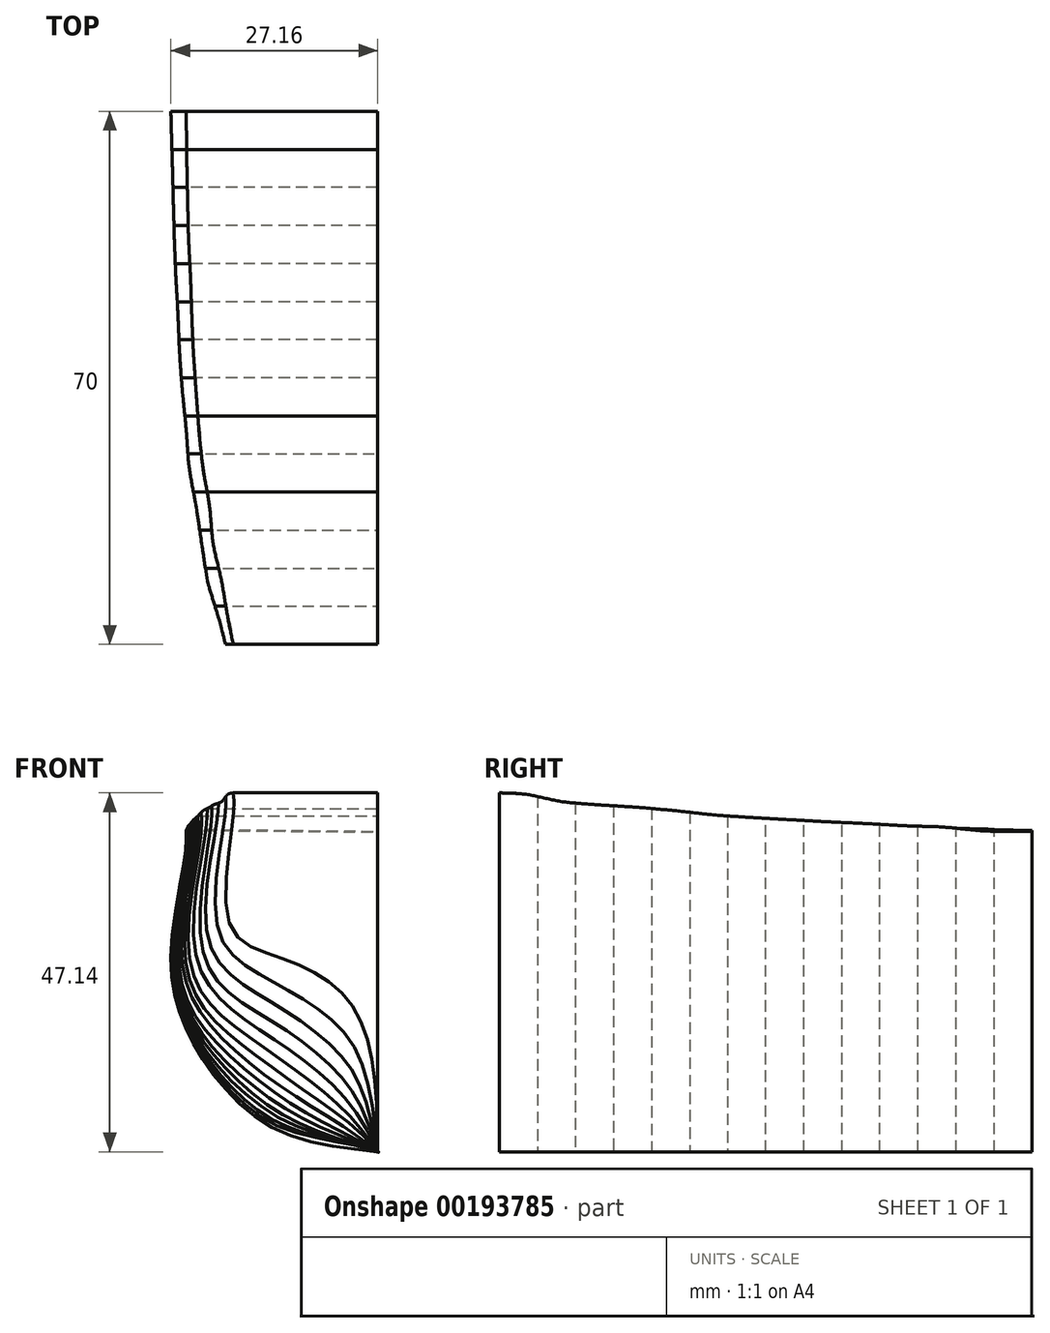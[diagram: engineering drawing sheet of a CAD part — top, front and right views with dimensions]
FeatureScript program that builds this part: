
annotation { "Feature Type Name" : "Feature", "Feature Type Description" : "" }
export const myFeature = defineFeature(function(context is Context, id is Id, definition is map)
    precondition{}
    {
        {
            var Q0;
            Q0=qCreatedBy(makeId("Front.planeOp"),FACE);
            var sketch = newSketch(context, id + "F0", { "sketchPlane" : qUnion([Q0])});
            skLineSegment(sketch, "E0", {"start": v(-1.24, 24.74) * mm, "end": v(-1.24, -22.4) * mm});
            skFitSpline(sketch, "E1", {"points": [v(-1.24, -22.4) * mm, v(-14.07, -19.7) * mm, v(-22.33, -12.84) * mm, v(-26.84, -5.13) * mm, v(-28.38, 3.95) * mm, v(-26.49, 16.94) * mm, v(-26.4, 19.83) * mm], "startDerivative": vector(-68.68, 7.38) * mm, "endDerivative": vector(-1.29, 24.48) * mm});
            skLineSegment(sketch, "E2", {"start": v(-26.4, 19.83) * mm, "end": v(-1.24, 19.58) * mm});
            skSolve(sketch);
        }
        {
            var Q0;
            Q0=qCreatedBy(makeId("Front.planeOp"),FACE);
            cPlane(context, id + "F1", {"entities" : qUnion([Q0]), "cplaneType" : CPlaneType.OFFSET, "offset" : 5 * mm, "width" : 150 * mm, "height" : 150 * mm});
        }
        {
            var Q0;
            Q0=qCreatedBy(id+"F1.planeOp",FACE);
            var sketch = newSketch(context, id + "F2", { "sketchPlane" : qUnion([Q0])});
            skLineSegment(sketch, "E3", {"start": v(-1.24, 24.74) * mm, "end": v(-1.24, -22.4) * mm});
            skFitSpline(sketch, "E4", {"points": [v(-1.24, -22.4) * mm, v(-13.68, -19.3) * mm, v(-22.09, -12.65) * mm, v(-26.68, -5.02) * mm, v(-28.23, 4.02) * mm, v(-26.4, 17.02) * mm, v(-26.33, 19.94) * mm], "startDerivative": vector(-61.26, 21.5) * mm, "endDerivative": vector(-1.44, 24.58) * mm});
            skLineSegment(sketch, "E5", {"start": v(-26.33, 19.94) * mm, "end": v(-1.24, 19.7) * mm});
            skSolve(sketch);
        }
        {
            var Q0;
            {var subQ0=sQuery(id+"F0.wireOp",EDGE,"E1");Q0=makeQuery(id+"F0.imprint","IMPRINT",FACE,{"disambiguationData":[TD([[makeQuery(id+"F0.imprint","IMPRINT",EDGE,{"derivedFrom":subQ0}),-1.0]])]});}
            var Q1;
            {var subQ0=sQuery(id+"F2.wireOp",EDGE,"E4");Q1=makeQuery(id+"F2.imprint","IMPRINT",FACE,{"disambiguationData":[TD([[makeQuery(id+"F2.imprint","IMPRINT",EDGE,{"derivedFrom":subQ0}),-1.0]])]});}
            loft(context, id + "F3", {"sheetProfilesArray" : [{ "sheetProfileEntities" : qUnion([Q0]) }, { "sheetProfileEntities" : qUnion([Q1]) }]});
        }
        {
            var Q0;
            Q0=qCreatedBy(id+"F1.planeOp",FACE);
            cPlane(context, id + "F4", {"entities" : qUnion([Q0]), "cplaneType" : CPlaneType.OFFSET, "offset" : 5 * mm, "width" : 150 * mm, "height" : 150 * mm});
        }
        {
            var Q0;
            Q0=qCreatedBy(id+"F4.planeOp",FACE);
            var sketch = newSketch(context, id + "F5", { "sketchPlane" : qUnion([Q0])});
            skLineSegment(sketch, "E6", {"start": v(-1.24, 24.74) * mm, "end": v(-1.24, -22.4) * mm});
            skFitSpline(sketch, "E7", {"points": [v(-1.24, -22.4) * mm, v(-13.39, -19) * mm, v(-21.77, -12.4) * mm, v(-26.53, -4.92) * mm, v(-28.1, 4.08) * mm, v(-26.3, 17.1) * mm, v(-26.23, 20.09) * mm], "startDerivative": vector(-61.65, 21.65) * mm, "endDerivative": vector(-1.33, 24.82) * mm});
            skLineSegment(sketch, "E8", {"start": v(-26.23, 20.09) * mm, "end": v(-1.24, 20.09) * mm});
            skSolve(sketch);
        }
        {
            var Q1;
            {var subQ0=sQuery(id+"F2.wireOp",EDGE,"E4");Q1=makeQuery(id+"F3.opLoft","CAP_FACE",FACE,{"disambiguationData":[OSD([makeQuery(id+"F2.imprint","IMPRINT",FACE,{"disambiguationData":[TD([[makeQuery(id+"F2.imprint","IMPRINT",EDGE,{"derivedFrom":subQ0}),-1.0]])]})])],"isStart":true});}
            var Q2;
            {var subQ0=sQuery(id+"F5.wireOp",EDGE,"E7");Q2=makeQuery(id+"F5.imprint","IMPRINT",FACE,{"disambiguationData":[TD([[makeQuery(id+"F5.imprint","IMPRINT",EDGE,{"derivedFrom":subQ0}),-1.0]])]});}
            loft(context, id + "F6", {"operationType" : NewBodyOperationType.ADD, "startCondition" : LoftEndDerivativeType.MATCH_CURVATURE, "startMagnitude" : 1, "sheetProfilesArray" : [{ "sheetProfileEntities" : qUnion([Q1]) }, { "sheetProfileEntities" : qUnion([Q2]) }]});
        }
        {
            var Q0;
            Q0=qCreatedBy(id+"F4.planeOp",FACE);
            cPlane(context, id + "F7", {"entities" : qUnion([Q0]), "cplaneType" : CPlaneType.OFFSET, "offset" : 5 * mm, "width" : 150 * mm, "height" : 150 * mm});
        }
        {
            var Q0;
            Q0=qCreatedBy(id+"F7.planeOp",FACE);
            var sketch = newSketch(context, id + "F8", { "sketchPlane" : qUnion([Q0])});
            skLineSegment(sketch, "E9", {"start": v(-1.24, 24.74) * mm, "end": v(-1.24, -22.4) * mm});
            skFitSpline(sketch, "E10", {"points": [v(-1.24, -22.4) * mm, v(-12.95, -18.55) * mm, v(-21.39, -12.08) * mm, v(-26.33, -4.78) * mm, v(-27.97, 4.13) * mm, v(-26.2, 17.21) * mm, v(-26.12, 20.36) * mm], "startDerivative": vector(-62.32, 21.88) * mm, "endDerivative": vector(-1.45, 25.67) * mm});
            skLineSegment(sketch, "E11", {"start": v(-26.12, 20.36) * mm, "end": v(-1.24, 20.36) * mm});
            skSolve(sketch);
        }
        {
            var Q1;
            {var subQ0=sQuery(id+"F5.wireOp",EDGE,"E7");Q1=makeQuery(id+"F6.opLoft","CAP_FACE",FACE,{"disambiguationData":[OSD([makeQuery(id+"F5.imprint","IMPRINT",FACE,{"disambiguationData":[TD([[makeQuery(id+"F5.imprint","IMPRINT",EDGE,{"derivedFrom":subQ0}),-1.0]])]})])],"isStart":true});}
            var Q2;
            {var subQ0=sQuery(id+"F8.wireOp",EDGE,"E10");Q2=makeQuery(id+"F8.imprint","IMPRINT",FACE,{"disambiguationData":[TD([[makeQuery(id+"F8.imprint","IMPRINT",EDGE,{"derivedFrom":subQ0}),-1.0]])]});}
            loft(context, id + "F9", {"operationType" : NewBodyOperationType.ADD, "startCondition" : LoftEndDerivativeType.MATCH_CURVATURE, "startMagnitude" : 1, "sheetProfilesArray" : [{ "sheetProfileEntities" : qUnion([Q1]) }, { "sheetProfileEntities" : qUnion([Q2]) }]});
        }
        {
            var Q0;
            Q0=qCreatedBy(id+"F7.planeOp",FACE);
            cPlane(context, id + "F10", {"entities" : qUnion([Q0]), "cplaneType" : CPlaneType.OFFSET, "offset" : 5 * mm, "width" : 150 * mm, "height" : 150 * mm});
        }
        {
            var Q0;
            Q0=qCreatedBy(id+"F10.planeOp",FACE);
            var sketch = newSketch(context, id + "F11", { "sketchPlane" : qUnion([Q0])});
            skLineSegment(sketch, "E12", {"start": v(-1.24, 24.74) * mm, "end": v(-1.24, -22.4) * mm});
            skFitSpline(sketch, "E13", {"points": [v(-1.24, -22.4) * mm, v(-12.54, -18.13) * mm, v(-20.94, -11.72) * mm, v(-26.08, -4.6) * mm, v(-27.8, 4.2) * mm, v(-26.01, 17.39) * mm, v(-25.9, 20.6) * mm], "startDerivative": vector(-62.84, 22.07) * mm, "endDerivative": vector(-1.04, 25.92) * mm});
            skLineSegment(sketch, "E14", {"start": v(-25.9, 20.6) * mm, "end": v(-1.24, 20.6) * mm});
            skSolve(sketch);
        }
        {
            var Q1;
            {var subQ0=sQuery(id+"F8.wireOp",EDGE,"E10");Q1=makeQuery(id+"F9.opLoft","CAP_FACE",FACE,{"disambiguationData":[OSD([makeQuery(id+"F8.imprint","IMPRINT",FACE,{"disambiguationData":[TD([[makeQuery(id+"F8.imprint","IMPRINT",EDGE,{"derivedFrom":subQ0}),-1.0]])]})])],"isStart":true});}
            var Q2;
            {var subQ0=sQuery(id+"F11.wireOp",EDGE,"E13");Q2=makeQuery(id+"F11.imprint","IMPRINT",FACE,{"disambiguationData":[TD([[makeQuery(id+"F11.imprint","IMPRINT",EDGE,{"derivedFrom":subQ0}),-1.0]])]});}
            loft(context, id + "F12", {"operationType" : NewBodyOperationType.ADD, "startCondition" : LoftEndDerivativeType.MATCH_CURVATURE, "startMagnitude" : 1, "sheetProfilesArray" : [{ "sheetProfileEntities" : qUnion([Q1]) }, { "sheetProfileEntities" : qUnion([Q2]) }]});
        }
        {
            var Q0;
            Q0=qCreatedBy(id+"F10.planeOp",FACE);
            cPlane(context, id + "F13", {"entities" : qUnion([Q0]), "cplaneType" : CPlaneType.OFFSET, "offset" : 5 * mm, "width" : 150 * mm, "height" : 150 * mm});
        }
        {
            var Q0;
            Q0=qCreatedBy(id+"F13.planeOp",FACE);
            var sketch = newSketch(context, id + "F14", { "sketchPlane" : qUnion([Q0])});
            skLineSegment(sketch, "E15", {"start": v(-1.24, 24.74) * mm, "end": v(-1.24, -22.4) * mm});
            skFitSpline(sketch, "E16", {"points": [v(-1.24, -22.4) * mm, v(-11.95, -17.53) * mm, v(-20.41, -11.29) * mm, v(-25.78, -4.4) * mm, v(-27.54, 4.32) * mm, v(-25.82, 17.59) * mm, v(-25.7, 20.85) * mm], "startDerivative": vector(-63.96, 28.52) * mm, "endDerivative": vector(-0.98, 26.03) * mm});
            skLineSegment(sketch, "E17", {"start": v(-25.7, 20.85) * mm, "end": v(-1.24, 20.85) * mm});
            skSolve(sketch);
        }
        {
            var Q1;
            {var subQ0=sQuery(id+"F11.wireOp",EDGE,"E13");Q1=makeQuery(id+"F12.opLoft","CAP_FACE",FACE,{"disambiguationData":[OSD([makeQuery(id+"F11.imprint","IMPRINT",FACE,{"disambiguationData":[TD([[makeQuery(id+"F11.imprint","IMPRINT",EDGE,{"derivedFrom":subQ0}),-1.0]])]})])],"isStart":true});}
            var Q2;
            {var subQ0=sQuery(id+"F14.wireOp",EDGE,"E16");Q2=makeQuery(id+"F14.imprint","IMPRINT",FACE,{"disambiguationData":[TD([[makeQuery(id+"F14.imprint","IMPRINT",EDGE,{"derivedFrom":subQ0}),-1.0]])]});}
            loft(context, id + "F15", {"operationType" : NewBodyOperationType.ADD, "startCondition" : LoftEndDerivativeType.MATCH_CURVATURE, "startMagnitude" : 1, "sheetProfilesArray" : [{ "sheetProfileEntities" : qUnion([Q1]) }, { "sheetProfileEntities" : qUnion([Q2]) }]});
        }
        {
            var Q0;
            Q0=qCreatedBy(id+"F13.planeOp",FACE);
            cPlane(context, id + "F16", {"entities" : qUnion([Q0]), "cplaneType" : CPlaneType.OFFSET, "offset" : 5 * mm, "width" : 150 * mm, "height" : 150 * mm});
        }
        {
            var Q0;
            Q0=qCreatedBy(id+"F16.planeOp",FACE);
            var sketch = newSketch(context, id + "F17", { "sketchPlane" : qUnion([Q0])});
            skLineSegment(sketch, "E18", {"start": v(-1.24, 24.74) * mm, "end": v(-1.24, -22.4) * mm});
            skFitSpline(sketch, "E19", {"points": [v(-1.24, -22.4) * mm, v(-11.33, -16.88) * mm, v(-19.67, -10.68) * mm, v(-25.44, -4.16) * mm, v(-27.32, 4.42) * mm, v(-25.6, 17.82) * mm, v(-25.51, 21.1) * mm], "startDerivative": vector(-62.63, 37.16) * mm, "endDerivative": vector(-1.25, 26.07) * mm});
            skLineSegment(sketch, "E20", {"start": v(-25.51, 21.1) * mm, "end": v(-1.24, 21.1) * mm});
            skSolve(sketch);
        }
        {
            var Q1;
            {var subQ0=sQuery(id+"F14.wireOp",EDGE,"E16");Q1=makeQuery(id+"F15.opLoft","CAP_FACE",FACE,{"disambiguationData":[OSD([makeQuery(id+"F14.imprint","IMPRINT",FACE,{"disambiguationData":[TD([[makeQuery(id+"F14.imprint","IMPRINT",EDGE,{"derivedFrom":subQ0}),-1.0]])]})])],"isStart":true});}
            var Q2;
            {var subQ0=sQuery(id+"F17.wireOp",EDGE,"E19");Q2=makeQuery(id+"F17.imprint","IMPRINT",FACE,{"disambiguationData":[TD([[makeQuery(id+"F17.imprint","IMPRINT",EDGE,{"derivedFrom":subQ0}),-1.0]])]});}
            loft(context, id + "F18", {"operationType" : NewBodyOperationType.ADD, "startCondition" : LoftEndDerivativeType.MATCH_CURVATURE, "startMagnitude" : 1, "sheetProfilesArray" : [{ "sheetProfileEntities" : qUnion([Q1]) }, { "sheetProfileEntities" : qUnion([Q2]) }]});
        }
        {
            var Q0;
            Q0=qCreatedBy(id+"F16.planeOp",FACE);
            cPlane(context, id + "F19", {"entities" : qUnion([Q0]), "cplaneType" : CPlaneType.OFFSET, "offset" : 5 * mm, "width" : 150 * mm, "height" : 150 * mm});
        }
        {
            var Q0;
            Q0=qCreatedBy(id+"F19.planeOp",FACE);
            var sketch = newSketch(context, id + "F20", { "sketchPlane" : qUnion([Q0])});
            skLineSegment(sketch, "E21", {"start": v(-1.24, 24.74) * mm, "end": v(-1.24, -22.4) * mm});
            skFitSpline(sketch, "E22", {"points": [v(-1.24, -22.4) * mm, v(-10.52, -16.06) * mm, v(-18.9, -10.05) * mm, v(-24.75, -3.68) * mm, v(-27.02, 4.55) * mm, v(-25.3, 18.05) * mm, v(-25.2, 21.39) * mm], "startDerivative": vector(-55.22, 46.4) * mm, "endDerivative": vector(-1.44, 26.07) * mm});
            skLineSegment(sketch, "E23", {"start": v(-25.2, 21.39) * mm, "end": v(-1.24, 21.39) * mm});
            skSolve(sketch);
        }
        {
            var Q1;
            {var subQ0=sQuery(id+"F17.wireOp",EDGE,"E19");Q1=makeQuery(id+"F18.opLoft","CAP_FACE",FACE,{"disambiguationData":[OSD([makeQuery(id+"F17.imprint","IMPRINT",FACE,{"disambiguationData":[TD([[makeQuery(id+"F17.imprint","IMPRINT",EDGE,{"derivedFrom":subQ0}),-1.0]])]})])],"isStart":true});}
            var Q2;
            {var subQ0=sQuery(id+"F20.wireOp",EDGE,"E22");Q2=makeQuery(id+"F20.imprint","IMPRINT",FACE,{"disambiguationData":[TD([[makeQuery(id+"F20.imprint","IMPRINT",EDGE,{"derivedFrom":subQ0}),-1.0]])]});}
            loft(context, id + "F21", {"operationType" : NewBodyOperationType.ADD, "startCondition" : LoftEndDerivativeType.MATCH_CURVATURE, "startMagnitude" : 1, "sheetProfilesArray" : [{ "sheetProfileEntities" : qUnion([Q1]) }, { "sheetProfileEntities" : qUnion([Q2]) }]});
        }
        {
            var Q0;
            Q0=qCreatedBy(id+"F19.planeOp",FACE);
            cPlane(context, id + "F22", {"entities" : qUnion([Q0]), "cplaneType" : CPlaneType.OFFSET, "offset" : 5 * mm, "width" : 150 * mm, "height" : 150 * mm});
        }
        {
            var Q0;
            Q0=qCreatedBy(id+"F22.planeOp",FACE);
            var sketch = newSketch(context, id + "F23", { "sketchPlane" : qUnion([Q0])});
            skLineSegment(sketch, "E24", {"start": v(-1.24, 24.74) * mm, "end": v(-1.24, -22.4) * mm});
            skLineSegment(sketch, "E25", {"start": v(-22.43, -12.92) * mm, "end": v(-7.08, -0.46) * mm, "construction": true});
            skLineSegment(sketch, "E26", {"start": v(-2.5, -7.82) * mm, "end": v(-14.13, -19.76) * mm, "construction": true});
            skLineSegment(sketch, "E27", {"start": v(-14.72, 3.3) * mm, "end": v(-26.84, -5.13) * mm, "construction": true});
            skLineSegment(sketch, "E28", {"start": v(-20.62, 7.4) * mm, "end": v(-28.47, 3.9) * mm, "construction": true});
            skLineSegment(sketch, "E29", {"start": v(-24.86, 21.7) * mm, "end": v(-1.24, 21.7) * mm});
            skFitSpline(sketch, "E30", {"points": [v(-24.86, 21.7) * mm, v(-24.86, 18.38) * mm, v(-26.55, 4.76) * mm, v(-24.21, -3.3) * mm, v(-17.9, -9.24) * mm, v(-9.66, -15.16) * mm, v(-1.24, -22.4) * mm], "startDerivative": vector(2.42, -25.82) * mm, "endDerivative": vector(41.84, -52.05) * mm});
            skSolve(sketch);
        }
        {
            var Q1;
            {var subQ0=sQuery(id+"F20.wireOp",EDGE,"E22");Q1=makeQuery(id+"F21.opLoft","CAP_FACE",FACE,{"disambiguationData":[OSD([makeQuery(id+"F20.imprint","IMPRINT",FACE,{"disambiguationData":[TD([[makeQuery(id+"F20.imprint","IMPRINT",EDGE,{"derivedFrom":subQ0}),-1.0]])]})])],"isStart":true});}
            var Q2;
            {var subQ2=sQuery(id+"F23.wireOp",EDGE,"E29");Q2=makeQuery(id+"F23.imprint","IMPRINT",FACE,{"disambiguationData":[TD([[makeQuery(id+"F23.imprint","IMPRINT",EDGE,{"derivedFrom":subQ2}),-1.0]])]});}
            loft(context, id + "F24", {"operationType" : NewBodyOperationType.ADD, "startCondition" : LoftEndDerivativeType.MATCH_CURVATURE, "startMagnitude" : 1, "sheetProfilesArray" : [{ "sheetProfileEntities" : qUnion([Q1]) }, { "sheetProfileEntities" : qUnion([Q2]) }]});
        }
        {
            var Q0;
            Q0=qCreatedBy(id+"F22.planeOp",FACE);
            cPlane(context, id + "F25", {"entities" : qUnion([Q0]), "cplaneType" : CPlaneType.OFFSET, "offset" : 5 * mm, "width" : 150 * mm, "height" : 150 * mm});
        }
        {
            var Q0;
            Q0=qCreatedBy(id+"F25.planeOp",FACE);
            var sketch = newSketch(context, id + "F26", { "sketchPlane" : qUnion([Q0])});
            skLineSegment(sketch, "E31", {"start": v(-1.24, 24.74) * mm, "end": v(-1.24, -22.4) * mm});
            skLineSegment(sketch, "E32", {"start": v(-24.4, 22.19) * mm, "end": v(-1.24, 22.19) * mm});
            skFitSpline(sketch, "E33", {"points": [v(-24.4, 22.19) * mm, v(-24.48, 18.75) * mm, v(-26.15, 5.25) * mm, v(-23.39, -2.81) * mm, v(-16.95, -8.12) * mm, v(-8.87, -14.11) * mm, v(-1.24, -22.4) * mm], "startDerivative": vector(1.66, -26.52) * mm, "endDerivative": vector(45.17, -68.41) * mm});
            skLineSegment(sketch, "E34", {"start": v(-22.43, -12.92) * mm, "end": v(-7.08, -0.46) * mm, "construction": true});
            skLineSegment(sketch, "E35", {"start": v(-2.5, -7.82) * mm, "end": v(-14.13, -19.76) * mm, "construction": true});
            skLineSegment(sketch, "E36", {"start": v(-14.72, 3.3) * mm, "end": v(-26.84, -5.13) * mm, "construction": true});
            skLineSegment(sketch, "E37", {"start": v(-20.62, 7.4) * mm, "end": v(-28.47, 3.9) * mm, "construction": true});
            skSolve(sketch);
        }
        {
            var Q1;
            {var subQ2=sQuery(id+"F23.wireOp",EDGE,"E29");Q1=makeQuery(id+"F24.opLoft","CAP_FACE",FACE,{"disambiguationData":[OSD([makeQuery(id+"F23.imprint","IMPRINT",FACE,{"disambiguationData":[TD([[makeQuery(id+"F23.imprint","IMPRINT",EDGE,{"derivedFrom":subQ2}),-1.0]])]})])],"isStart":true});}
            var Q2;
            {var subQ2=sQuery(id+"F26.wireOp",EDGE,"E32");Q2=makeQuery(id+"F26.imprint","IMPRINT",FACE,{"disambiguationData":[TD([[makeQuery(id+"F26.imprint","IMPRINT",EDGE,{"derivedFrom":subQ2}),-1.0]])]});}
            loft(context, id + "F27", {"operationType" : NewBodyOperationType.ADD, "startCondition" : LoftEndDerivativeType.MATCH_CURVATURE, "startMagnitude" : 1, "sheetProfilesArray" : [{ "sheetProfileEntities" : qUnion([Q1]) }, { "sheetProfileEntities" : qUnion([Q2]) }]});
        }
        {
            var Q0;
            Q0=qCreatedBy(id+"F25.planeOp",FACE);
            cPlane(context, id + "F28", {"entities" : qUnion([Q0]), "cplaneType" : CPlaneType.OFFSET, "offset" : 5 * mm, "width" : 150 * mm, "height" : 150 * mm});
        }
        {
            var Q0;
            Q0=qCreatedBy(id+"F28.planeOp",FACE);
            var sketch = newSketch(context, id + "F29", { "sketchPlane" : qUnion([Q0])});
            skLineSegment(sketch, "E38", {"start": v(-1.24, 24.74) * mm, "end": v(-1.24, -22.4) * mm});
            skLineSegment(sketch, "E39", {"start": v(-23.61, 22.68) * mm, "end": v(-1.24, 22.68) * mm});
            skFitSpline(sketch, "E40", {"points": [v(-23.61, 22.68) * mm, v(-23.9, 19.3) * mm, v(-25.38, 5.6) * mm, v(-22.19, -2.03) * mm, v(-15.57, -7.14) * mm, v(-7.78, -13.02) * mm, v(-1.24, -22.4) * mm], "startDerivative": vector(-0.8, -25.86) * mm, "endDerivative": vector(30.6, -70.37) * mm});
            skLineSegment(sketch, "E41", {"start": v(-22.43, -12.92) * mm, "end": v(-7.08, -0.46) * mm, "construction": true});
            skLineSegment(sketch, "E42", {"start": v(-2.5, -7.82) * mm, "end": v(-14.13, -19.76) * mm, "construction": true});
            skLineSegment(sketch, "E43", {"start": v(-14.72, 3.3) * mm, "end": v(-26.84, -5.13) * mm, "construction": true});
            skLineSegment(sketch, "E44", {"start": v(-20.62, 7.4) * mm, "end": v(-28.47, 3.9) * mm, "construction": true});
            skSolve(sketch);
        }
        {
            var Q1;
            {var subQ2=sQuery(id+"F26.wireOp",EDGE,"E32");Q1=makeQuery(id+"F27.opLoft","CAP_FACE",FACE,{"disambiguationData":[OSD([makeQuery(id+"F26.imprint","IMPRINT",FACE,{"disambiguationData":[TD([[makeQuery(id+"F26.imprint","IMPRINT",EDGE,{"derivedFrom":subQ2}),-1.0]])]})])],"isStart":true});}
            var Q2;
            {var subQ2=sQuery(id+"F29.wireOp",EDGE,"E39");Q2=makeQuery(id+"F29.imprint","IMPRINT",FACE,{"disambiguationData":[TD([[makeQuery(id+"F29.imprint","IMPRINT",EDGE,{"derivedFrom":subQ2}),-1.0]])]});}
            loft(context, id + "F30", {"operationType" : NewBodyOperationType.ADD, "startCondition" : LoftEndDerivativeType.MATCH_CURVATURE, "startMagnitude" : 1, "sheetProfilesArray" : [{ "sheetProfileEntities" : qUnion([Q1]) }, { "sheetProfileEntities" : qUnion([Q2]) }]});
        }
        {
            var Q0;
            Q0=qCreatedBy(id+"F28.planeOp",FACE);
            cPlane(context, id + "F31", {"entities" : qUnion([Q0]), "cplaneType" : CPlaneType.OFFSET, "offset" : 5 * mm, "width" : 150 * mm, "height" : 150 * mm});
        }
        {
            var Q0;
            Q0=qCreatedBy(id+"F31.planeOp",FACE);
            var sketch = newSketch(context, id + "F32", { "sketchPlane" : qUnion([Q0])});
            skLineSegment(sketch, "E45", {"start": v(-1.24, 24.74) * mm, "end": v(-1.24, -22.4) * mm});
            skFitSpline(sketch, "E46", {"points": [v(-23.04, 23.04) * mm, v(-23.22, 19.7) * mm, v(-24.53, 5.97) * mm, v(-21.09, -1.2) * mm, v(-14.04, -5.94) * mm, v(-6.6, -11.95) * mm, v(-1.24, -22.4) * mm], "startDerivative": vector(1.12, -25.93) * mm, "endDerivative": vector(24.55, -84.95) * mm});
            skLineSegment(sketch, "E47", {"start": v(-23.04, 23.04) * mm, "end": v(-1.24, 23.04) * mm});
            skLineSegment(sketch, "E48", {"start": v(-22.43, -12.92) * mm, "end": v(-7.08, -0.46) * mm, "construction": true});
            skLineSegment(sketch, "E49", {"start": v(-2.5, -7.82) * mm, "end": v(-14.13, -19.76) * mm, "construction": true});
            skLineSegment(sketch, "E50", {"start": v(-14.72, 3.3) * mm, "end": v(-26.84, -5.13) * mm, "construction": true});
            skLineSegment(sketch, "E51", {"start": v(-20.62, 7.4) * mm, "end": v(-28.47, 3.9) * mm, "construction": true});
            skSolve(sketch);
        }
        {
            var Q1;
            {var subQ2=sQuery(id+"F29.wireOp",EDGE,"E39");Q1=makeQuery(id+"F30.opLoft","CAP_FACE",FACE,{"disambiguationData":[OSD([makeQuery(id+"F29.imprint","IMPRINT",FACE,{"disambiguationData":[TD([[makeQuery(id+"F29.imprint","IMPRINT",EDGE,{"derivedFrom":subQ2}),-1.0]])]})])],"isStart":true});}
            var Q2;
            {var subQ0=sQuery(id+"F32.wireOp",EDGE,"E46");Q2=makeQuery(id+"F32.imprint","IMPRINT",FACE,{"disambiguationData":[TD([[makeQuery(id+"F32.imprint","IMPRINT",EDGE,{"derivedFrom":subQ0}),1.0]])]});}
            loft(context, id + "F33", {"operationType" : NewBodyOperationType.ADD, "startCondition" : LoftEndDerivativeType.MATCH_CURVATURE, "startMagnitude" : 1, "sheetProfilesArray" : [{ "sheetProfileEntities" : qUnion([Q1]) }, { "sheetProfileEntities" : qUnion([Q2]) }]});
        }
        {
            var Q0;
            Q0=qCreatedBy(id+"F31.planeOp",FACE);
            cPlane(context, id + "F34", {"entities" : qUnion([Q0]), "cplaneType" : CPlaneType.OFFSET, "offset" : 5 * mm, "width" : 150 * mm, "height" : 150 * mm});
        }
        {
            var Q0;
            Q0=qCreatedBy(id+"F34.planeOp",FACE);
            var sketch = newSketch(context, id + "F35", { "sketchPlane" : qUnion([Q0])});
            skLineSegment(sketch, "E52", {"start": v(-1.24, 24.74) * mm, "end": v(-1.24, -22.4) * mm});
            skLineSegment(sketch, "E53", {"start": v(-22.11, 23.4) * mm, "end": v(-1.24, 23.4) * mm});
            skFitSpline(sketch, "E54", {"points": [v(-22.11, 23.4) * mm, v(-22.44, 20.36) * mm, v(-23.66, 6.36) * mm, v(-19.33, -0.12) * mm, v(-12.38, -4.5) * mm, v(-5.43, -10.54) * mm, v(-1.24, -22.4) * mm], "startDerivative": vector(-1.05, -25.13) * mm, "endDerivative": vector(17.98, -94.55) * mm});
            skLineSegment(sketch, "E55", {"start": v(-22.43, -12.92) * mm, "end": v(-7.08, -0.46) * mm, "construction": true});
            skLineSegment(sketch, "E56", {"start": v(-2.5, -7.82) * mm, "end": v(-14.13, -19.76) * mm, "construction": true});
            skLineSegment(sketch, "E57", {"start": v(-14.72, 3.3) * mm, "end": v(-26.84, -5.13) * mm, "construction": true});
            skLineSegment(sketch, "E58", {"start": v(-20.62, 7.4) * mm, "end": v(-28.47, 3.9) * mm, "construction": true});
            skSolve(sketch);
        }
        {
            var Q1;
            {var subQ0=sQuery(id+"F32.wireOp",EDGE,"E46");Q1=makeQuery(id+"F33.opLoft","CAP_FACE",FACE,{"disambiguationData":[OSD([makeQuery(id+"F32.imprint","IMPRINT",FACE,{"disambiguationData":[TD([[makeQuery(id+"F32.imprint","IMPRINT",EDGE,{"derivedFrom":subQ0}),1.0]])]})])],"isStart":true});}
            var Q2;
            {var subQ2=sQuery(id+"F35.wireOp",EDGE,"E53");Q2=makeQuery(id+"F35.imprint","IMPRINT",FACE,{"disambiguationData":[TD([[makeQuery(id+"F35.imprint","IMPRINT",EDGE,{"derivedFrom":subQ2}),-1.0]])]});}
            loft(context, id + "F36", {"operationType" : NewBodyOperationType.ADD, "startCondition" : LoftEndDerivativeType.MATCH_CURVATURE, "startMagnitude" : 1, "sheetProfilesArray" : [{ "sheetProfileEntities" : qUnion([Q1]) }, { "sheetProfileEntities" : qUnion([Q2]) }]});
        }
        {
            var Q0;
            Q0=qCreatedBy(id+"F34.planeOp",FACE);
            cPlane(context, id + "F37", {"entities" : qUnion([Q0]), "cplaneType" : CPlaneType.OFFSET, "offset" : 5 * mm, "width" : 150 * mm, "height" : 150 * mm});
        }
        {
            var Q0;
            Q0=qCreatedBy(id+"F37.planeOp",FACE);
            var sketch = newSketch(context, id + "F38", { "sketchPlane" : qUnion([Q0])});
            skLineSegment(sketch, "E59", {"start": v(-1.24, 24.74) * mm, "end": v(-1.24, -22.4) * mm});
            skLineSegment(sketch, "E60", {"start": v(-21.17, 24.26) * mm, "end": v(-1.24, 24.26) * mm});
            skFitSpline(sketch, "E61", {"points": [v(-21.17, 24.26) * mm, v(-21.4, 20.87) * mm, v(-22.23, 6.92) * mm, v(-17.26, 1.23) * mm, v(-10.22, -2.9) * mm, v(-3.99, -9.22) * mm, v(-1.24, -22.4) * mm], "startDerivative": vector(0, -25.12) * mm, "endDerivative": vector(6.88, -70.79) * mm});
            skLineSegment(sketch, "E62", {"start": v(-22.43, -12.92) * mm, "end": v(-7.08, -0.46) * mm, "construction": true});
            skLineSegment(sketch, "E63", {"start": v(-2.5, -7.82) * mm, "end": v(-14.13, -19.76) * mm, "construction": true});
            skLineSegment(sketch, "E64", {"start": v(-14.72, 3.3) * mm, "end": v(-26.84, -5.13) * mm, "construction": true});
            skLineSegment(sketch, "E65", {"start": v(-20.62, 7.4) * mm, "end": v(-28.47, 3.9) * mm, "construction": true});
            skSolve(sketch);
        }
        {
            var Q1;
            {var subQ2=sQuery(id+"F35.wireOp",EDGE,"E53");Q1=makeQuery(id+"F36.opLoft","CAP_FACE",FACE,{"disambiguationData":[OSD([makeQuery(id+"F35.imprint","IMPRINT",FACE,{"disambiguationData":[TD([[makeQuery(id+"F35.imprint","IMPRINT",EDGE,{"derivedFrom":subQ2}),-1.0]])]})])],"isStart":true});}
            var Q2;
            {var subQ2=sQuery(id+"F38.wireOp",EDGE,"E60");Q2=makeQuery(id+"F38.imprint","IMPRINT",FACE,{"disambiguationData":[TD([[makeQuery(id+"F38.imprint","IMPRINT",EDGE,{"derivedFrom":subQ2}),-1.0]])]});}
            loft(context, id + "F39", {"operationType" : NewBodyOperationType.ADD, "startCondition" : LoftEndDerivativeType.MATCH_CURVATURE, "startMagnitude" : 1, "sheetProfilesArray" : [{ "sheetProfileEntities" : qUnion([Q1]) }, { "sheetProfileEntities" : qUnion([Q2]) }]});
        }
        {
            var Q0;
            Q0=qCreatedBy(id+"F37.planeOp",FACE);
            cPlane(context, id + "F40", {"entities" : qUnion([Q0]), "cplaneType" : CPlaneType.OFFSET, "offset" : 5 * mm, "width" : 150 * mm, "height" : 150 * mm});
        }
        {
            var Q0;
            Q0=qCreatedBy(id+"F40.planeOp",FACE);
            var sketch = newSketch(context, id + "F41", { "sketchPlane" : qUnion([Q0])});
            skLineSegment(sketch, "E66", {"start": v(-20.2, 24.74) * mm, "end": v(-1.24, 24.74) * mm});
            skLineSegment(sketch, "E67", {"start": v(-1.24, 24.74) * mm, "end": v(-1.24, -22.4) * mm});
            skFitSpline(sketch, "E68", {"points": [v(-20.2, 24.74) * mm, v(-20.2, 21.6) * mm, v(-20.62, 7.4) * mm, v(-14.72, 3.3) * mm, v(-7.08, -0.46) * mm, v(-2.5, -7.82) * mm, v(-1.24, -22.4) * mm], "startDerivative": vector(2.48, -23.21) * mm, "endDerivative": vector(0.84, -73.75) * mm});
            skLineSegment(sketch, "E69", {"start": v(-22.43, -12.92) * mm, "end": v(-7.08, -0.46) * mm, "construction": true});
            skLineSegment(sketch, "E70", {"start": v(-2.5, -7.82) * mm, "end": v(-14.13, -19.76) * mm, "construction": true});
            skLineSegment(sketch, "E71", {"start": v(-14.72, 3.3) * mm, "end": v(-26.84, -5.13) * mm, "construction": true});
            skLineSegment(sketch, "E72", {"start": v(-20.62, 7.4) * mm, "end": v(-28.47, 3.9) * mm, "construction": true});
            skSolve(sketch);
        }
        {
            var Q0;
            Q0=qCreatedBy(id+"F40.planeOp",FACE);
            cPlane(context, id + "F42", {"entities" : qUnion([Q0]), "cplaneType" : CPlaneType.OFFSET, "offset" : 5 * mm, "width" : 150 * mm, "height" : 150 * mm});
        }
        {
            var Q1;
            {var subQ2=sQuery(id+"F38.wireOp",EDGE,"E60");Q1=makeQuery(id+"F39.opLoft","CAP_FACE",FACE,{"disambiguationData":[OSD([makeQuery(id+"F38.imprint","IMPRINT",FACE,{"disambiguationData":[TD([[makeQuery(id+"F38.imprint","IMPRINT",EDGE,{"derivedFrom":subQ2}),-1.0]])]})])],"isStart":true});}
            var Q2;
            Q2=makeQuery(id+"F41.imprint","IMPRINT",FACE,{"disambiguationData":[TD([[makeQuery(id+"F41.imprint","IMPRINT",EDGE,{"derivedFrom":sQuery(id+"F41.wireOp",EDGE,"E66")}),-1.0]])]});
            loft(context, id + "F43", {"operationType" : NewBodyOperationType.ADD, "startCondition" : LoftEndDerivativeType.MATCH_CURVATURE, "startMagnitude" : 1, "sheetProfilesArray" : [{ "sheetProfileEntities" : qUnion([Q1]) }, { "sheetProfileEntities" : qUnion([Q2]) }]});
        }
    });
